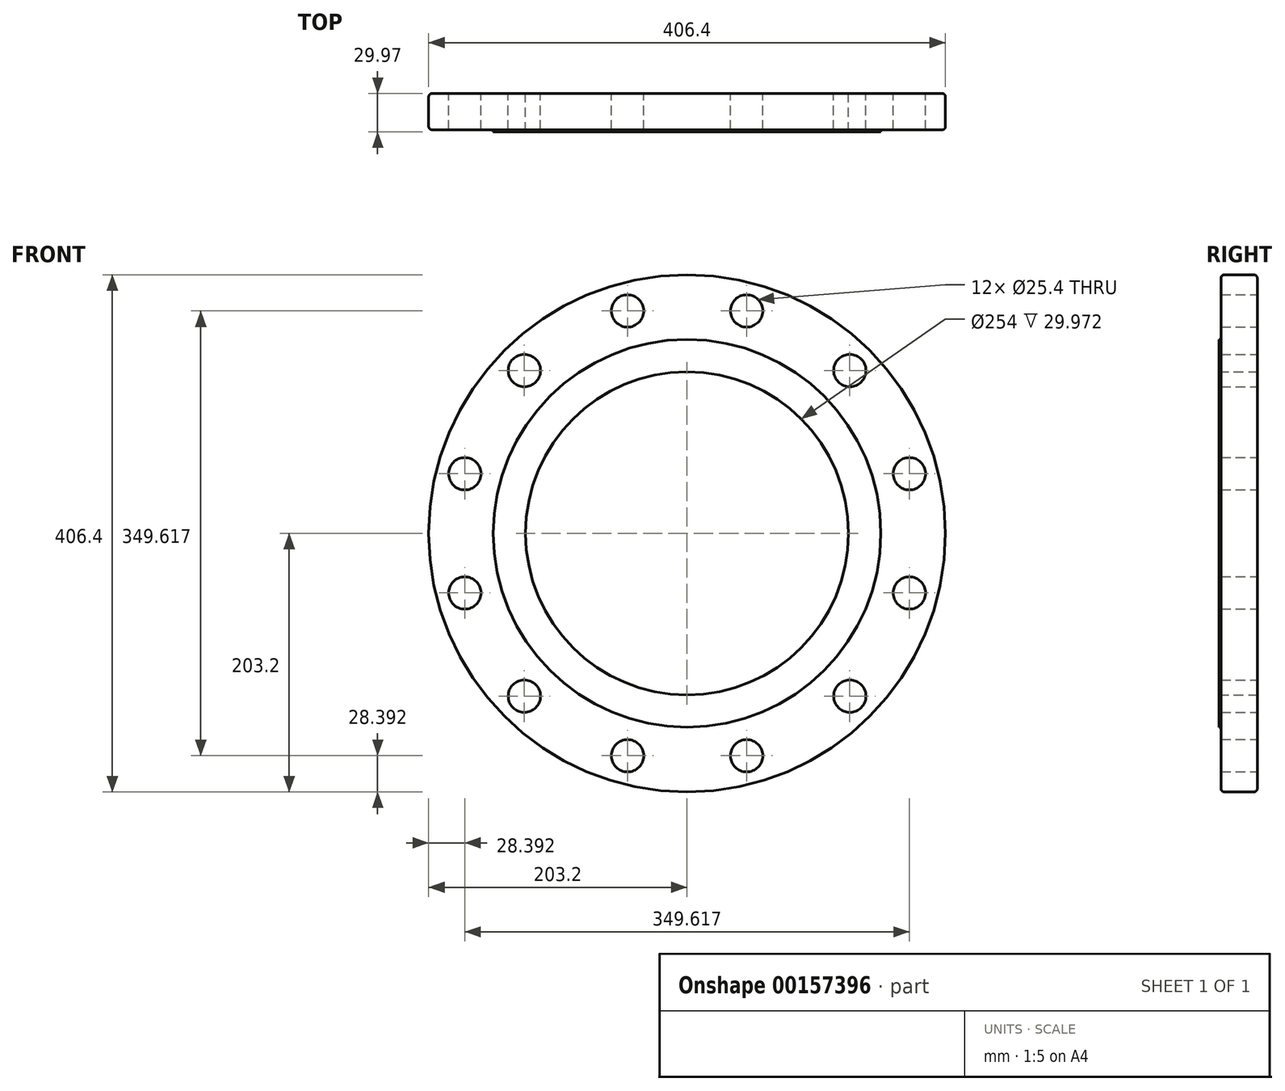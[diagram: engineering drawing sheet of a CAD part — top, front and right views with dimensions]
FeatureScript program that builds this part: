
annotation { "Feature Type Name" : "Feature", "Feature Type Description" : "" }
export const myFeature = defineFeature(function(context is Context, id is Id, definition is map)
    precondition{}
    {
        {
            var Q0;
            Q0=qCreatedBy(makeId("Front.planeOp"),FACE);
            var sketch = newSketch(context, id + "F0", { "sketchPlane" : qUnion([Q0])});
            skCircle(sketch, "E0", {"center": v(0, 0) * mm, "radius": 203.2 * mm});
            skCircle(sketch, "E1", {"center": v(0, 0) * mm, "radius": 127 * mm});
            skLineSegment(sketch, "E2", {"start": v(0, 0) * mm, "end": v(0, 225.6) * mm});
            skLineSegment(sketch, "E3", {"start": v(0, 0) * mm, "end": v(59.02, 220.25) * mm});
            skCircle(sketch, "E4", {"center": v(46.84, 174.8) * mm, "radius": 12.7 * mm});
            skCircle(sketch, "E5.1.0", {"center": v(-46.84, 174.8) * mm, "radius": 12.7 * mm});
            skCircle(sketch, "E5.2.0", {"center": v(-127.97, 127.97) * mm, "radius": 12.7 * mm});
            skCircle(sketch, "E5.3.0", {"center": v(-174.8, 46.84) * mm, "radius": 12.7 * mm});
            skCircle(sketch, "E5.4.0", {"center": v(-174.8, -46.84) * mm, "radius": 12.7 * mm});
            skCircle(sketch, "E5.5.0", {"center": v(-127.97, -127.97) * mm, "radius": 12.7 * mm});
            skCircle(sketch, "E5.6.0", {"center": v(-46.84, -174.8) * mm, "radius": 12.7 * mm});
            skCircle(sketch, "E5.7.0", {"center": v(46.84, -174.8) * mm, "radius": 12.7 * mm});
            skCircle(sketch, "E5.8.0", {"center": v(127.97, -127.97) * mm, "radius": 12.7 * mm});
            skCircle(sketch, "E5.9.0", {"center": v(174.8, -46.84) * mm, "radius": 12.7 * mm});
            skCircle(sketch, "E5.10.0", {"center": v(174.8, 46.84) * mm, "radius": 12.7 * mm});
            skCircle(sketch, "E5.11.0", {"center": v(127.97, 127.97) * mm, "radius": 12.7 * mm});
            skSolve(sketch);
        }
        {
            var Q0;
            Q0 = qSketchRegion(id + "F0", true);
            extrude(context, id + "F1", {"entities" : qUnion([Q0]), "depth" : 28.45 * mm});
        }
        {
            var Q0;
            Q0=makeQuery(id+"F1.opExtrude","CAP_EDGE",EDGE,{"disambiguationData":[OSD([sQuery(id+"F0.wireOp",EDGE,"E0")])],"isStart":false});
            var Q1;
            Q1=makeQuery(id+"F1.opExtrude","CAP_EDGE",EDGE,{"disambiguationData":[OSD([sQuery(id+"F0.wireOp",EDGE,"E0")])],"isStart":true});
            fillet(context, id + "F2", {"entities" : qUnion([Q0, Q1]), "radius" : 2.54 * mm, "tangentPropagation" : true, "allowEdgeOverflow" : false});
        }
        {
            var Q0;
            Q0=makeQuery(id+"F1.opExtrude","CAP_FACE",FACE,{"disambiguationData":[OSD([sQuery(id+"F0.wireOp",EDGE,"E0"),sQuery(id+"F0.wireOp",EDGE,"E1"),sQuery(id+"F0.wireOp",EDGE,"E4"),sQuery(id+"F0.wireOp",EDGE,"E5.1.0"),sQuery(id+"F0.wireOp",EDGE,"E5.2.0"),sQuery(id+"F0.wireOp",EDGE,"E5.3.0"),sQuery(id+"F0.wireOp",EDGE,"E5.4.0"),sQuery(id+"F0.wireOp",EDGE,"E5.5.0"),sQuery(id+"F0.wireOp",EDGE,"E5.6.0"),sQuery(id+"F0.wireOp",EDGE,"E5.7.0"),sQuery(id+"F0.wireOp",EDGE,"E5.8.0"),sQuery(id+"F0.wireOp",EDGE,"E5.9.0"),sQuery(id+"F0.wireOp",EDGE,"E5.10.0"),sQuery(id+"F0.wireOp",EDGE,"E5.11.0")])],"isStart":false});
            var sketch = newSketch(context, id + "F3", { "sketchPlane" : qUnion([Q0])});
            skCircle(sketch, "E6", {"center": v(0, 0) * mm, "radius": 152.4 * mm});
            skCircle(sketch, "E7", {"center": v(0, 0) * mm, "radius": 127 * mm});
            skSolve(sketch);
        }
        {
            var Q0;
            Q0 = qSketchRegion(id + "F3", true);
            extrude(context, id + "F4", {"entities" : qUnion([Q0]), "operationType" : NewBodyOperationType.ADD, "depth" : 1.52 * mm});
        }
    });
